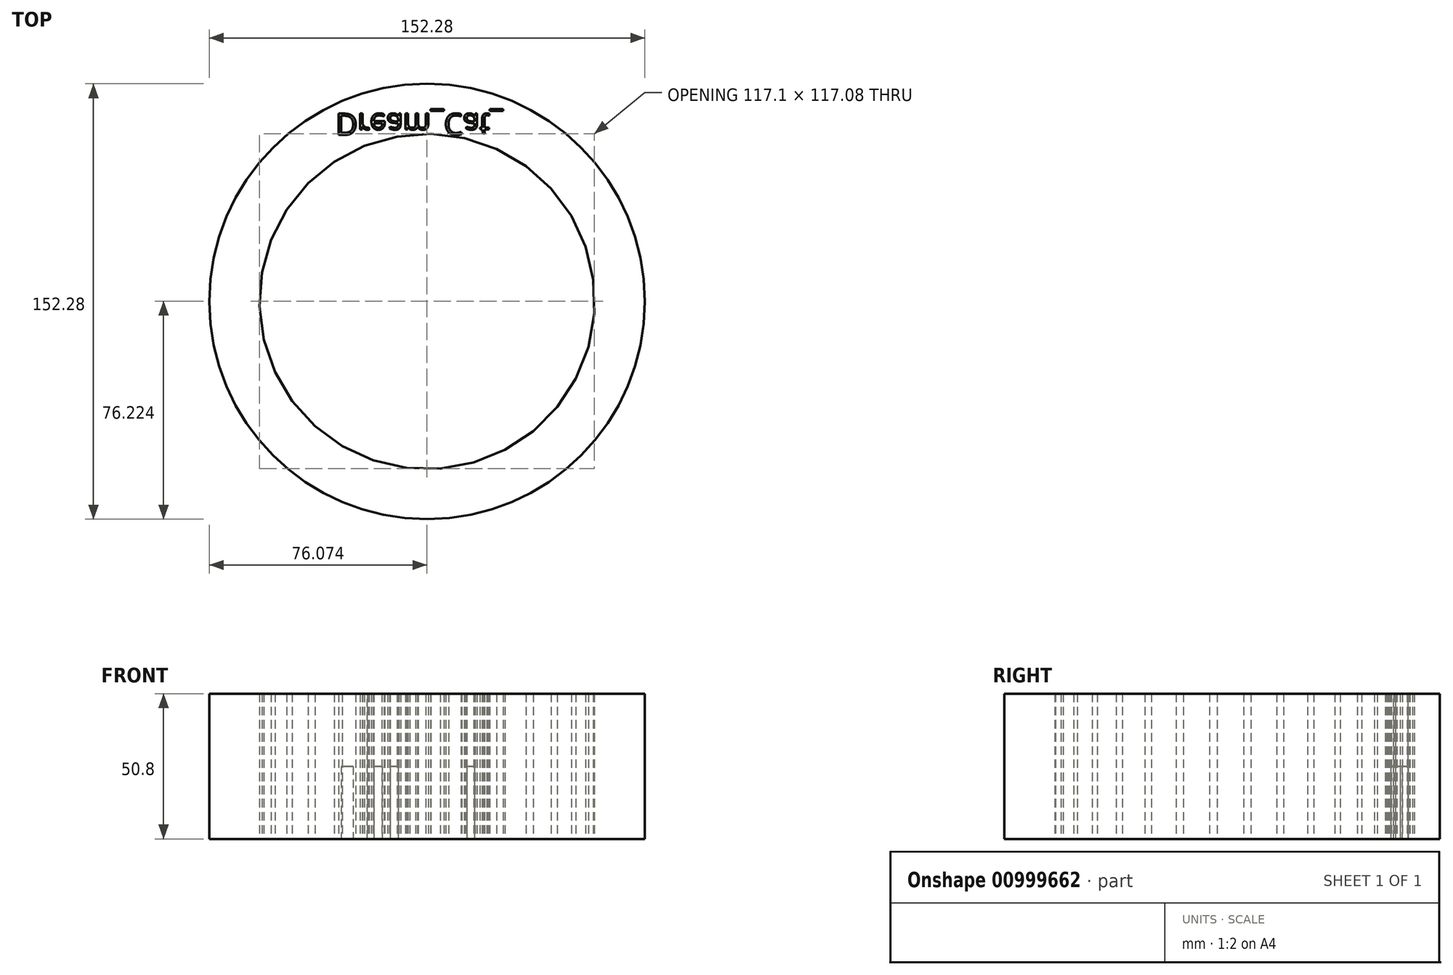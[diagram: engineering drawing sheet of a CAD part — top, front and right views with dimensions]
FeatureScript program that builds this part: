
annotation { "Feature Type Name" : "Feature", "Feature Type Description" : "" }
export const myFeature = defineFeature(function(context is Context, id is Id, definition is map)
    precondition{}
    {
        {
            var Q0;
            Q0=qCreatedBy(makeId("Top.planeOp"),FACE);
            var sketch = newSketch(context, id + "F0", { "sketchPlane" : qUnion([Q0])});
            skCircle(sketch, "E0", {"center": v(0, 0) * mm, "radius": 76.14 * mm});
            skSolve(sketch);
        }
        {
            var Q0;
            Q0=makeQuery(id+"F0.imprint","IMPRINT",FACE,{"disambiguationData":[TD([[makeQuery(id+"F0.imprint","IMPRINT",EDGE,{"derivedFrom":sQuery(id+"F0.wireOp",EDGE,"E0")}),1.0]])]});
            extrude(context, id + "F1", {"entities" : qUnion([Q0]), "depth" : 25.4 * mm, "offsetDistance" : 25.4 * mm});
        }
        {
            var Q0;
            Q0=makeQuery(id+"F1.opExtrude","CAP_FACE",FACE,{"disambiguationData":[OSD([sQuery(id+"F0.wireOp",EDGE,"E0")])],"isStart":true});
            var sketch = newSketch(context, id + "F2", { "sketchPlane" : qUnion([Q0])});
            skText(sketch, "E1", { "text": "Dream_Cat_", "fontName": "OpenSans-Regular.ttf"});
            const initialGuessF2  = {"E1": [-0.03191, -0.0657, 1, 0, 0.0075]};
            skSetInitialGuess(sketch, initialGuessF2);
            skSolve(sketch);
        }
        {
            var Q0;
            Q0 = qSketchRegion(id + "F2", true);
            extrude(context, id + "F3", {"entities" : qUnion([Q0]), "operationType" : NewBodyOperationType.REMOVE, "oppositeDirection" : true, "depth" : 25.4 * mm, "offsetDistance" : 25.4 * mm});
        }
        {
            var Q0;
            {var subQ0=sQuery(id+"F0.wireOp",EDGE,"E0");Q0=makeQuery(id+"F3.boolean.opBoolean","SPLIT",FACE,{"disambiguationData":[TD([makeQuery(id+"F1.opExtrude","SWEPT_FACE",FACE,{"disambiguationData":[OSD([subQ0])]})])],"derivedFrom":makeQuery(id+"F1.opExtrude","CAP_FACE",FACE,{"disambiguationData":[OSD([subQ0])],"isStart":false})});}
            extrude(context, id + "F4", {"entities" : qUnion([Q0]), "operationType" : NewBodyOperationType.ADD, "depth" : 25.4 * mm, "offsetDistance" : 25.4 * mm});
        }
        {
            var Q0;
            {var subQ0=sQuery(id+"F0.wireOp",EDGE,"E0");Q0=makeQuery(id+"F3.boolean.opBoolean","SPLIT",FACE,{"disambiguationData":[TD([makeQuery(id+"F1.opExtrude","SWEPT_FACE",FACE,{"disambiguationData":[OSD([subQ0])]})])],"derivedFrom":makeQuery(id+"F1.opExtrude","CAP_FACE",FACE,{"disambiguationData":[OSD([subQ0])],"isStart":true})});}
            var sketch = newSketch(context, id + "F5", { "sketchPlane" : qUnion([Q0])});
            skCircle(sketch, "E2.cCircle", {"center": v(0, 0) * mm, "radius": 58.34 * mm, "construction": true});
            skLineSegment(sketch, "E2.0", {"start": v(34.57, -47.37) * mm, "end": v(24.32, -53.36) * mm});
            skLineSegment(sketch, "E2.1", {"start": v(24.32, -53.36) * mm, "end": v(13.09, -57.16) * mm});
            skLineSegment(sketch, "E2.2", {"start": v(13.09, -57.16) * mm, "end": v(1.31, -58.63) * mm});
            skLineSegment(sketch, "E2.3", {"start": v(1.31, -58.63) * mm, "end": v(-10.52, -57.69) * mm});
            skLineSegment(sketch, "E2.4", {"start": v(-10.52, -57.69) * mm, "end": v(-21.91, -54.4) * mm});
            skLineSegment(sketch, "E2.5", {"start": v(-21.91, -54.4) * mm, "end": v(-32.42, -48.87) * mm});
            skLineSegment(sketch, "E2.6", {"start": v(-32.42, -48.87) * mm, "end": v(-41.59, -41.34) * mm});
            skLineSegment(sketch, "E2.7", {"start": v(-41.59, -41.34) * mm, "end": v(-49.06, -32.12) * mm});
            skLineSegment(sketch, "E2.8", {"start": v(-49.06, -32.12) * mm, "end": v(-54.52, -21.6) * mm});
            skLineSegment(sketch, "E2.9", {"start": v(-54.52, -21.6) * mm, "end": v(-57.75, -10.17) * mm});
            skLineSegment(sketch, "E2.10", {"start": v(-57.75, -10.17) * mm, "end": v(-58.62, 1.66) * mm});
            skLineSegment(sketch, "E2.11", {"start": v(-58.62, 1.66) * mm, "end": v(-57.08, 13.43) * mm});
            skLineSegment(sketch, "E2.12", {"start": v(-57.08, 13.43) * mm, "end": v(-53.21, 24.64) * mm});
            skLineSegment(sketch, "E2.13", {"start": v(-53.21, 24.64) * mm, "end": v(-47.16, 34.85) * mm});
            skLineSegment(sketch, "E2.14", {"start": v(-47.16, 34.85) * mm, "end": v(-39.18, 43.63) * mm});
            skLineSegment(sketch, "E2.15", {"start": v(-39.18, 43.63) * mm, "end": v(-29.6, 50.62) * mm});
            skLineSegment(sketch, "E2.16", {"start": v(-29.6, 50.62) * mm, "end": v(-18.8, 55.55) * mm});
            skLineSegment(sketch, "E2.17", {"start": v(-18.8, 55.55) * mm, "end": v(-7.24, 58.2) * mm});
            skLineSegment(sketch, "E2.18", {"start": v(-7.24, 58.2) * mm, "end": v(4.63, 58.46) * mm});
            skLineSegment(sketch, "E2.19", {"start": v(4.63, 58.46) * mm, "end": v(16.3, 56.33) * mm});
            skLineSegment(sketch, "E2.20", {"start": v(16.3, 56.33) * mm, "end": v(27.3, 51.9) * mm});
            skLineSegment(sketch, "E2.21", {"start": v(27.3, 51.9) * mm, "end": v(37.2, 45.34) * mm});
            skLineSegment(sketch, "E2.22", {"start": v(37.2, 45.34) * mm, "end": v(45.56, 36.92) * mm});
            skLineSegment(sketch, "E2.23", {"start": v(45.56, 36.92) * mm, "end": v(52.06, 27) * mm});
            skLineSegment(sketch, "E2.24", {"start": v(52.06, 27) * mm, "end": v(56.43, 15.96) * mm});
            skLineSegment(sketch, "E2.25", {"start": v(56.43, 15.96) * mm, "end": v(58.48, 4.28) * mm});
            skLineSegment(sketch, "E2.26", {"start": v(58.48, 4.28) * mm, "end": v(58.15, -7.58) * mm});
            skLineSegment(sketch, "E2.27", {"start": v(58.15, -7.58) * mm, "end": v(55.43, -19.13) * mm});
            skLineSegment(sketch, "E2.28", {"start": v(55.43, -19.13) * mm, "end": v(50.45, -29.9) * mm});
            skLineSegment(sketch, "E2.29", {"start": v(50.45, -29.9) * mm, "end": v(43.4, -39.44) * mm});
            skLineSegment(sketch, "E2.30", {"start": v(43.4, -39.44) * mm, "end": v(34.57, -47.37) * mm});
            skPoint(sketch, "E2.0.midPoint", {"position": v(29.45, -50.36) * mm});
            skSolve(sketch);
        }
        {
            var Q0;
            Q0=makeQuery(id+"F5.imprint","IMPRINT",FACE,{"disambiguationData":[TD([[makeQuery(id+"F5.imprint","IMPRINT",EDGE,{"derivedFrom":sQuery(id+"F5.wireOp",EDGE,"E2.0")}),-1.0]])]});
            extrude(context, id + "F6", {"entities" : qUnion([Q0]), "operationType" : NewBodyOperationType.REMOVE, "oppositeDirection" : true, "depth" : 25.4 * mm, "offsetDistance" : 25.4 * mm});
        }
        {
            var Q0;
            Q0=makeQuery(id+"F6.boolean.opBoolean","COPY",FACE,{"derivedFrom":makeQuery(id+"F6.opExtrude","CAP_FACE",FACE,{"disambiguationData":[OSD([sQuery(id+"F5.wireOp",EDGE,"E2.0"),sQuery(id+"F5.wireOp",EDGE,"E2.1"),sQuery(id+"F5.wireOp",EDGE,"E2.2"),sQuery(id+"F5.wireOp",EDGE,"E2.3"),sQuery(id+"F5.wireOp",EDGE,"E2.4"),sQuery(id+"F5.wireOp",EDGE,"E2.5"),sQuery(id+"F5.wireOp",EDGE,"E2.6"),sQuery(id+"F5.wireOp",EDGE,"E2.7"),sQuery(id+"F5.wireOp",EDGE,"E2.8"),sQuery(id+"F5.wireOp",EDGE,"E2.9"),sQuery(id+"F5.wireOp",EDGE,"E2.10"),sQuery(id+"F5.wireOp",EDGE,"E2.11"),sQuery(id+"F5.wireOp",EDGE,"E2.12"),sQuery(id+"F5.wireOp",EDGE,"E2.13"),sQuery(id+"F5.wireOp",EDGE,"E2.14"),sQuery(id+"F5.wireOp",EDGE,"E2.15"),sQuery(id+"F5.wireOp",EDGE,"E2.16"),sQuery(id+"F5.wireOp",EDGE,"E2.17"),sQuery(id+"F5.wireOp",EDGE,"E2.18"),sQuery(id+"F5.wireOp",EDGE,"E2.19"),sQuery(id+"F5.wireOp",EDGE,"E2.20"),sQuery(id+"F5.wireOp",EDGE,"E2.21"),sQuery(id+"F5.wireOp",EDGE,"E2.22"),sQuery(id+"F5.wireOp",EDGE,"E2.23"),sQuery(id+"F5.wireOp",EDGE,"E2.24"),sQuery(id+"F5.wireOp",EDGE,"E2.25"),sQuery(id+"F5.wireOp",EDGE,"E2.26"),sQuery(id+"F5.wireOp",EDGE,"E2.27"),sQuery(id+"F5.wireOp",EDGE,"E2.28"),sQuery(id+"F5.wireOp",EDGE,"E2.29"),sQuery(id+"F5.wireOp",EDGE,"E2.30")])],"isStart":false})});
            extrude(context, id + "F7", {"entities" : qUnion([Q0]), "operationType" : NewBodyOperationType.REMOVE, "oppositeDirection" : true, "depth" : 25.4 * mm, "offsetDistance" : 25.4 * mm});
        }
    });
